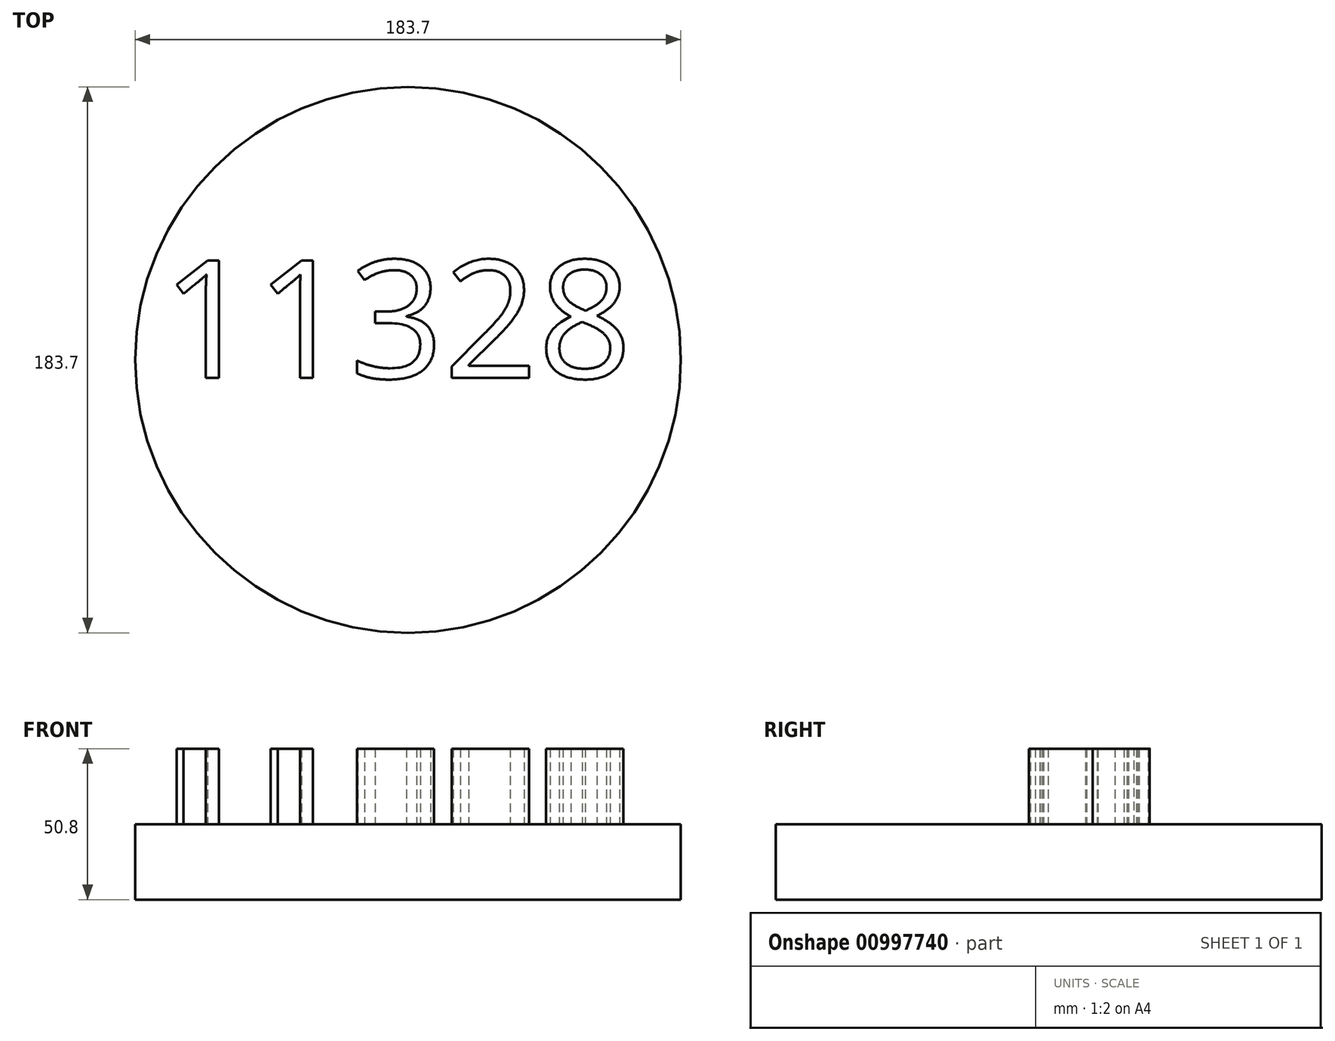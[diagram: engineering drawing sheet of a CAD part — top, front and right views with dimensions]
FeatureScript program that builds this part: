
annotation { "Feature Type Name" : "Feature", "Feature Type Description" : "" }
export const myFeature = defineFeature(function(context is Context, id is Id, definition is map)
    precondition{}
    {
        {
            var Q0;
            Q0=qCreatedBy(makeId("Top.planeOp"),FACE);
            var sketch = newSketch(context, id + "F0", { "sketchPlane" : qUnion([Q0])});
            skCircle(sketch, "E0", {"center": v(0, 0) * mm, "radius": 91.85 * mm});
            skSolve(sketch);
        }
        {
            var Q0;
            Q0=makeQuery(id+"F0.imprint","IMPRINT",FACE,{"disambiguationData":[TD([[makeQuery(id+"F0.imprint","IMPRINT",EDGE,{"derivedFrom":sQuery(id+"F0.wireOp",EDGE,"E0")}),1.0]])]});
            extrude(context, id + "F1", {"entities" : qUnion([Q0]), "depth" : 25.4 * mm, "offsetDistance" : 25.4 * mm});
        }
        {
            var Q0;
            Q0=makeQuery(id+"F1.opExtrude","CAP_FACE",FACE,{"disambiguationData":[OSD([sQuery(id+"F0.wireOp",EDGE,"E0")])],"isStart":false});
            var sketch = newSketch(context, id + "F2", { "sketchPlane" : qUnion([Q0])});
            skText(sketch, "E1", { "text": "11328\n\n", "fontName": "OpenSans-Regular.ttf"});
            const initialGuessF2  = {"E1": [-0.08301, -0.0061, 1, 0, 0.0399]};
            skSetInitialGuess(sketch, initialGuessF2);
            skSolve(sketch);
        }
        {
            var Q0;
            Q0 = qSketchRegion(id + "F2", true);
            extrude(context, id + "F3", {"entities" : qUnion([Q0]), "operationType" : NewBodyOperationType.ADD, "depth" : 25.4 * mm, "offsetDistance" : 25.4 * mm});
        }
    });
